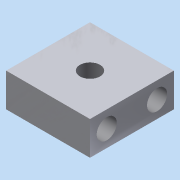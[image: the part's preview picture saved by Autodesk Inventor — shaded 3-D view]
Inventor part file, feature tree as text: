
AUTODESK INVENTOR PART (.ipt)
format: ipt  version: 2015 (Build 190159000, 159)  size: 103,936 bytes
history: native  units: in
note: dims shown in document units (in); Inventor stores cm internally (conversion verified against a paired STEP export)
features: sketch x3, hole x2, extrude x1
ambient origin geometry x8: Origin, YZ Plane, XZ Plane, XY Plane, X Axis, Y Axis, Z Axis, Center Point
bodies: Solid1 (feature_tree)
feature tree (6):
  extrude  "Extrusion1"  Depth=1.9685in
  hole  "Hole1"  [1 undecoded]
  hole  "Hole2"  [1 undecoded]
  sketch  "Sketch1"  dims[d0=1.9685in d1=1.9685in]
  sketch  "Sketch2"  dims[d2=0.7874in d3=0.0in d4=0.3937in]
  sketch  "Sketch3"  dims[d5=0.3937in d6=0.3937in d7=0.3937in d8=0.4724in d9=0.2362in d10=0.1575in d11=0.0787in d12=90.0deg d13=1.9685in d14=0.8108in d15=0.9843in d16=0.9843in d17=0.4724in d18=0.2362in d19=0.1575in d20=0.0787in d21=90.0deg d22=1.9685in d23=0.8108in]
note: 2 required parameter values undecoded (feature->parameter linkage not recoverable at this tier; creation-order binding heuristic only, values carry confidence <= 0.55)
